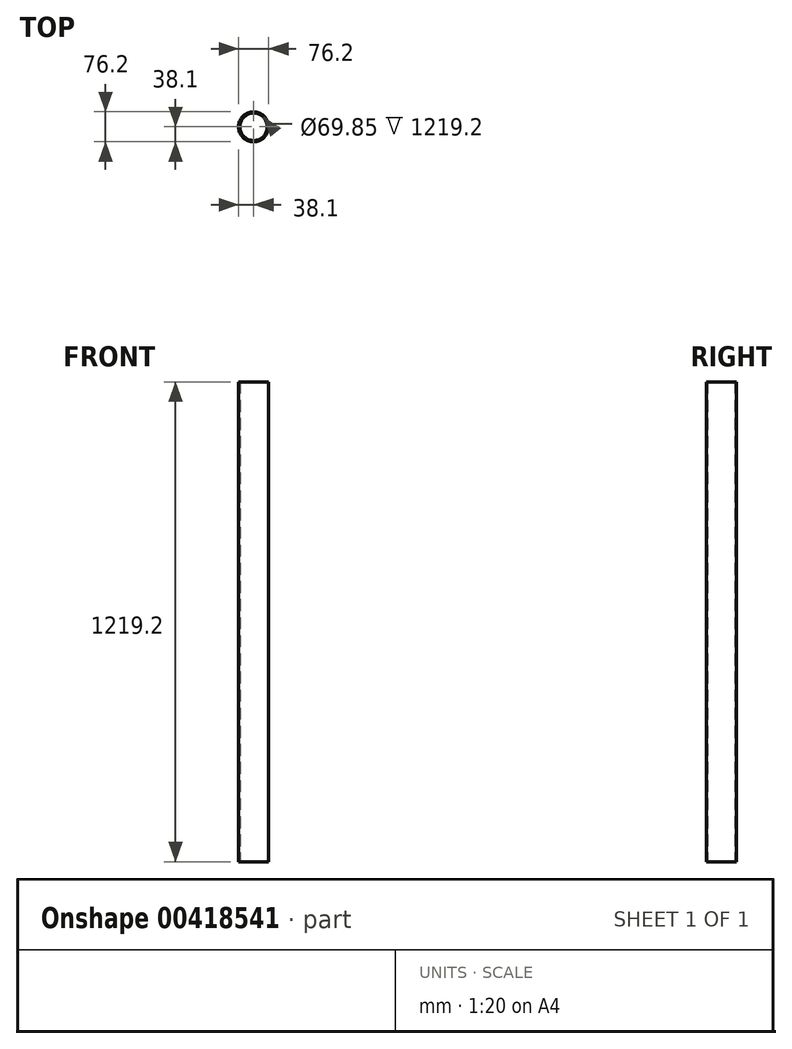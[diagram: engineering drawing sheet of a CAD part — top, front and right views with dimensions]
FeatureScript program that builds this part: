
annotation { "Feature Type Name" : "Feature", "Feature Type Description" : "" }
export const myFeature = defineFeature(function(context is Context, id is Id, definition is map)
    precondition{}
    {
        {
            var Q0;
            Q0=qCreatedBy(makeId("Top.planeOp"),FACE);
            var sketch = newSketch(context, id + "F0", { "sketchPlane" : qUnion([Q0])});
            skCircle(sketch, "E0", {"center": v(0, 0) * mm, "radius": 38.1 * mm});
            skCircle(sketch, "E1", {"center": v(0, 0) * mm, "radius": 34.93 * mm});
            skSolve(sketch);
        }
        {
            var Q0;
            Q0=makeQuery(id+"F0.imprint","IMPRINT",FACE,{"disambiguationData":[TD([[makeQuery(id+"F0.imprint","IMPRINT",EDGE,{"derivedFrom":sQuery(id+"F0.wireOp",EDGE,"E0")}),1.0]])]});
            extrude(context, id + "F1", {"entities" : qUnion([Q0]), "depth" : 1219.2 * mm});
        }
    });
